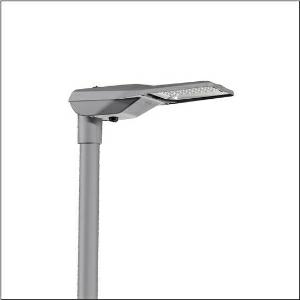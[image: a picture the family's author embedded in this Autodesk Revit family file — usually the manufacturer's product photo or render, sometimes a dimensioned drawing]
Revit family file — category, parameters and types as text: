
# Revit family: streetlight_sl_21_mini___st0_5a_5xe2b43t08gb_315d
name_source: partatom
category: Lighting Fixtures
units: mm (PartAtom-declared; Revit-internal decimal feet)

## family parameters
Cut with Voids When Loaded = No
Host = Face
Light Source = No
Part Type = Normal
Room Calculation Point = No
Round Connector Dimension = Use Diameter
Shared = No

## types (1)
- --- (1 x LED, 6180 lm, 40.4 W, 4000K)
    Apparent Load = 40 VA
    CIE Flux Codes = 41 75 97 100 100
    Color Rendering = 70
    Color Temperature = 4000K
    Default Elevation = 1800 mm
    Description = Streetlight SL 21 mini, mast luminaire, primary light control with lens, of PMMA, primary optical cover: cover, of toughened safety glass, transparent, light distribution: ST0.5a, light emission: direct distribution, primary light characteristic: asymmetric, installation type: side-entry, post-top, LED, High Power LED, rated luminous flux: 6.180lm, luminous efficacy: 153lm/W, light colour: 740, colour temperature: 4000K, control gear: D4i, control: overheat protection, constant luminous flux control, time-dependent luminous flux control, flexible luminous flux parameterisation, pre-setting: logarithmic dimming characteristic, mains connection: 220..240V, AC, 50/60Hz, start of lifetime: 40W, end of service life: 41W, reduction: 19W, luminaire housing, of diecast aluminium, powder-coated, Siteco® metallic grey (DB 702S), corrosivity category C5 mid according to DIN EN ISO 12944, please order mast flange separately, inclination adjustable: 0°, 5°, 10°, 15°, sealing non-destructively replaceable, multi-level sealing system, length: 628mm, width: 235mm, height: 110mm, mast flange for spigot size: 42mm (side-entry): 5XC10008XM4, 60/48mm (side-entry/post-top): 5XC10108XM2, 76/60mm (side-entry/post-top): 5XC10108XM1, mounting height: 4..8m, Smart Interface below and above, protection rating (complete): IP66, insulation class (complete): insulation class II (safety insulation), certification: CE, ENEC, ENEC+, VDE, impact resistance: IK10, permissible operating ambient temperature for outdoor applications: -40..+50°C, standard-compliant lighting for roads and squares, packaging unit: 1 piece

Light Distribution: ST0.5a
    Height = 110 mm
    Lamp = 1 x LED
    Lamp Light Flux = 6180 lm
    Lamp Power = 40.4 W
    Lamp count = 1
    Length = 625 mm
    Luminous efficacy = 153 lm/W
    Manufacturer = Siteco
    ModVariant = No
    Model = 5XE2B43T08GB
    Number of Poles = 1
    OnlyDefault = Yes
    Power Factor = 1
    Product Name = Streetlight SL 21 mini | ST0.5a
    Product group = mast luminaire | pylon top
    ProductGroupID = 6100
    Protection Class = Protection class II
    Protection Degree = IP 66
    RLX_Detail_Level = 1
    RLX_Emergency_Light_Flux = 0 lm
    RLX_Emergency_Type = 0
    RLX_Emergency_Type_DB = No
    RlxData = <blob elided: 37197 chars, md5=05fd3a20>
    Socket = socket
    Standby Power = 0 W
    System Light Flux = 6180 lm
    System Power = 40 W
    Type Comments = factory setting: luminous flux: 100 % | dim-lin: 254 | 812 mA
    Type Image = l_1003514.jpg
    URL = http://relux.com
    VarID = @adj_212375
    Voltage = 0 V
    Weight = 0.00 kg
    Width = 234 mm

## geometry (parser evidence)
native form markers: Blend x4, Sweep x9
no freeform markers — native parametric forms only
